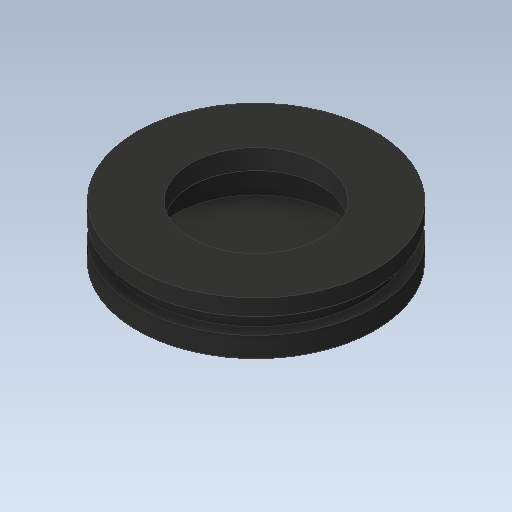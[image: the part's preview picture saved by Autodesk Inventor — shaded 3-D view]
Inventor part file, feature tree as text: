
AUTODESK INVENTOR PART (.ipt)
format: ipt  version: 2020 (Build 240168000, 168)  size: 140,800 bytes
history: native  units: mm
features: revolve x2, sketch x2
ambient origin geometry x8: Origin, YZ Plane, XZ Plane, XY Plane, X Axis, Y Axis, Z Axis, Center Point
bodies: Solid1 (feature_tree)
feature tree (4):
  revolve  "Revolution1"  [1 undecoded]
  revolve  "Revolution2"  [1 undecoded]
  sketch  "Sketch1"  dims[d0=3.490659mm d1=10.0mm]
  sketch  "Sketch2"  dims[d2=1.5mm d3=1.5mm d4=1.85mm d5=11.0mm d6=90.0deg d7=6.0mm d8=3.0mm d9=7.5mm d10=3.0mm d11=6.0mm d12=90.0deg]
note: 2 required parameter values undecoded (feature->parameter linkage not recoverable at this tier; creation-order binding heuristic only, values carry confidence <= 0.55)
